# Revit family: Lighting - Auberge Single Candelabra
name_source: partatom
category: Lighting Fixtures
revit_build: Autodesk Revit 2018 (Build: 20170927_1515(x64)
units: mm (PartAtom-declared; Revit-internal decimal feet)

## family parameters
Always vertical = Yes
Cut with Voids When Loaded = No
Host = Wall
Light Source = Yes
OmniClass Number = 23.80.70.00
OmniClass Title = Lighting
Part Type = Normal
Room Calculation Point = No
Round Connector Dimension = Use Diameter
Shared = No

## types (3) — shared parameters
Color Filter = 16777215
Description = LED Candelabra Wall Sconce
Dimming Lamp Color Temperature Shift = <None>
Emit from Line Length = 2' - 0"
Keynote = X
Manufacturer = Auberge Lighting
Shade Tag = CO-7W7H
Tilt Angle = 0.00°
URL = https://www.aubergelighting.com

## per-type parameters (varying)
| type | Apparent Load | Bracket Finish | Lamp | Model | Photometric Web File | Shade Finish |
| Island Breeze & Brass | 20 VA | AU Enviro Satin Brass | 2x 10W LED | AU-C10W-30-8-CO7W7H-IB-DE1A-ESB | generic | AU Island Breeze |
| Linear Cross & Bronze | 20 VA | AU Enviro Bronze | 2x 10W LED | AU-C10W-30-8-CO7W7H-LCV-DE1A-E0B | generic | AU Linear Cross |
| Rain & Nickel | 10 VA | AU Enviro Satin Nickel | 10W LED | AU-C10W-30-8-CO7W7H-RV-DE1A-ESN | Auberge C10W sconces.ies | AU Rain |

## geometry (parser evidence)
native form markers: Sweep x15
no freeform markers — native parametric forms only
